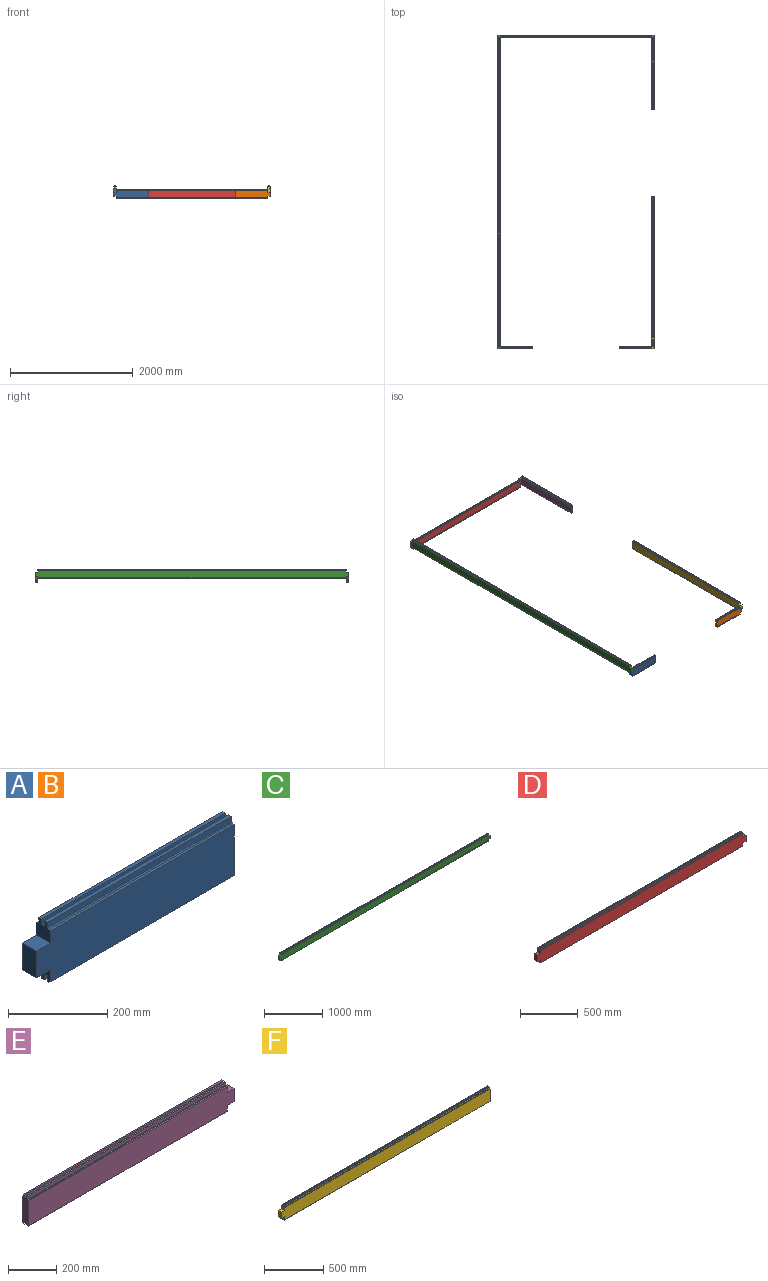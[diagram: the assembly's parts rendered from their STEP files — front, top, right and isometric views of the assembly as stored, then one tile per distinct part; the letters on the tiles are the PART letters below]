
ASSEMBLY  parts=6 mates=16
PART A: 30 faces, bbox 565x40x146 mm
  f0: plane 66x40mm, normal (-1,0,0), area 2640mm2, adj f1,f13,f27,f29
  f1: plane 565x126mm, normal (0,-1,0), area 68790mm2, adj f0,f2,f24,f25,f26,f27,f28,f29
  f2: plane 525x3mm, normal (0,-0.71,-0.71), area 2227.4mm2, adj f1,f3,f25,f26
  f3: plane 525x5mm, normal (0,0,-1), area 2625mm2, adj f2,f4,f25,f26
  f4: plane 525x14mm, normal (0,1,0), area 7350mm2, adj f3,f5,f25,f26
  f5: plane 525x8mm, normal (0,0,-1), area 4200mm2, adj f4,f6,f25,f26
  f6: plane 525x14mm, normal (0,-1,0), area 7350mm2, adj f5,f7,f25,f26
  f7: plane 525x8mm, normal (0,0,-1), area 4200mm2, adj f6,f8,f25,f26
  f8: plane 525x14mm, normal (0,1,0), area 7350mm2, adj f7,f9,f25,f26
  f9: plane 525x8mm, normal (0,0,-1), area 4200mm2, adj f8,f10,f25,f26
  f10: plane 525x14mm, normal (0,-1,0), area 7350mm2, adj f9,f11,f25,f26
  f11: plane 525x5mm, normal (0,0,-1), area 2625mm2, adj f10,f12,f25,f26
  f12: plane 525x3mm, normal (0,0.71,-0.71), area 2227.4mm2, adj f11,f13,f25,f26
  f13: plane 565x126mm, normal (0,1,0), area 68790mm2, adj f0,f12,f14,f25,f26,f27,f28,f29
  f14: plane 525x3mm, normal (0,0.71,0.71), area 2227.4mm2, adj f13,f15,f25,f28
  f15: plane 525x5mm, normal (0,0,1), area 2625mm2, adj f14,f16,f25,f28
  f16: plane 525x14mm, normal (0,1,0), area 7350mm2, adj f15,f17,f25,f28
  f17: plane 525x8mm, normal (0,0,1), area 4200mm2, adj f16,f18,f25,f28
  f18: plane 525x14mm, normal (0,-1,0), area 7350mm2, adj f17,f19,f25,f28
  f19: plane 525x8mm, normal (0,0,1), area 4200mm2, adj f18,f20,f25,f28
  f20: plane 525x14mm, normal (0,1,0), area 7350mm2, adj f19,f21,f25,f28
  f21: plane 525x8mm, normal (0,0,1), area 4200mm2, adj f20,f22,f25,f28
  f22: plane 525x14mm, normal (0,-1,0), area 7350mm2, adj f21,f23,f25,f28
  f23: plane 525x5mm, normal (0,0,1), area 2625mm2, adj f22,f24,f25,f28
  f24: plane 525x3mm, normal (0,-0.71,0.71), area 2227.4mm2, adj f1,f23,f25,f28
  f25: plane 146x40mm, normal (1,0,0), area 5262mm2, adj f1,f2,f3,f4,f5,f6,f7,f8
  f26: plane 40x33mm, normal (-1,0,0), area 1087mm2, adj f1,f2,f3,f4,f5,f6,f7,f8
  f27: plane 40x40mm, normal (0,0,-1), area 1600mm2, adj f0,f1,f13,f26
  f28: plane 47x40mm, normal (-1,0,0), area 1535mm2, adj f1,f13,f14,f15,f16,f17,f18,f19
  f29: plane 40x40mm, normal (0,0,1), area 1600mm2, adj f0,f1,f13,f28
PART B: same geometry as A
PART C: 34 faces, bbox 5100x40x146 mm
  f0: plane 5100x126mm, normal (0,1,0), area 637800mm2, adj f1,f23,f24,f25,f26,f27,f28,f29
  f1: plane 5020x3mm, normal (0,0.71,0.71), area 21298.1mm2, adj f0,f2,f26,f32
  f2: plane 5020x5mm, normal (0,0,1), area 25100mm2, adj f1,f3,f26,f32
  f3: plane 5020x14mm, normal (0,1,0), area 70280mm2, adj f2,f4,f26,f32
  f4: plane 5020x8mm, normal (0,0,1), area 40160mm2, adj f3,f5,f26,f32
  f5: plane 5020x14mm, normal (0,-1,0), area 70280mm2, adj f4,f6,f26,f32
  f6: plane 5020x8mm, normal (0,0,1), area 40160mm2, adj f5,f7,f26,f32
  f7: plane 5020x14mm, normal (0,1,0), area 70280mm2, adj f6,f8,f26,f32
  f8: plane 5020x8mm, normal (0,0,1), area 40160mm2, adj f7,f9,f26,f32
  f9: plane 5020x14mm, normal (0,-1,0), area 70280mm2, adj f8,f10,f26,f32
  f10: plane 5020x5mm, normal (0,0,1), area 25100mm2, adj f9,f11,f26,f32
  f11: plane 5020x3mm, normal (0,-0.71,0.71), area 21298.1mm2, adj f10,f12,f26,f32
  f12: plane 5100x126mm, normal (0,-1,0), area 637800mm2, adj f11,f13,f24,f25,f26,f27,f28,f29
  f13: plane 5020x3mm, normal (0,-0.71,-0.71), area 21298.1mm2, adj f12,f14,f28,f30
  f14: plane 5020x5mm, normal (0,0,-1), area 25100mm2, adj f13,f15,f28,f30
  f15: plane 5020x14mm, normal (0,1,0), area 70280mm2, adj f14,f16,f28,f30
  f16: plane 5020x8mm, normal (0,0,-1), area 40160mm2, adj f15,f17,f28,f30
  f17: plane 5020x14mm, normal (0,-1,0), area 70280mm2, adj f16,f18,f28,f30
  f18: plane 5020x8mm, normal (0,0,-1), area 40160mm2, adj f17,f19,f28,f30
  f19: plane 5020x14mm, normal (0,1,0), area 70280mm2, adj f18,f20,f28,f30
  f20: plane 5020x8mm, normal (0,0,-1), area 40160mm2, adj f19,f21,f28,f30
  f21: plane 5020x14mm, normal (0,-1,0), area 70280mm2, adj f20,f22,f28,f30
  f22: plane 5020x5mm, normal (0,0,-1), area 25100mm2, adj f21,f23,f28,f30
  f23: plane 5020x3mm, normal (0,0.71,-0.71), area 21298.1mm2, adj f0,f22,f28,f30
  f24: plane 66x40mm, normal (1,0,0), area 2640mm2, adj f0,f12,f31,f33
  f25: plane 66x40mm, normal (-1,0,0), area 2640mm2, adj f0,f12,f27,f29
  f26: plane 47x40mm, normal (-1,0,0), area 1535mm2, adj f0,f1,f2,f3,f4,f5,f6,f7
  f27: plane 40x40mm, normal (0,0,1), area 1600mm2, adj f0,f12,f25,f26
  f28: plane 40x33mm, normal (-1,0,0), area 1087mm2, adj f0,f12,f13,f14,f15,f16,f17,f18
  f29: plane 40x40mm, normal (0,0,-1), area 1600mm2, adj f0,f12,f25,f28
  f30: plane 40x33mm, normal (1,0,0), area 1087mm2, adj f0,f12,f13,f14,f15,f16,f17,f18
  f31: plane 40x40mm, normal (0,0,-1), area 1600mm2, adj f0,f12,f24,f30
  f32: plane 47x40mm, normal (1,0,0), area 1535mm2, adj f0,f1,f2,f3,f4,f5,f6,f7
  f33: plane 40x40mm, normal (0,0,1), area 1600mm2, adj f0,f12,f24,f32
PART D: 34 faces, bbox 2550x40x146 mm
  f0: plane 2550x126mm, normal (0,1,0), area 316500mm2, adj f1,f13,f14,f25,f26,f27,f28,f29
  f1: plane 2470x3mm, normal (0,0.71,0.71), area 10479.3mm2, adj f0,f2,f27,f33
  f2: plane 2470x5mm, normal (0,0,1), area 12350mm2, adj f1,f3,f27,f33
  f3: plane 2470x14mm, normal (0,1,0), area 34580mm2, adj f2,f4,f27,f33
  f4: plane 2470x8mm, normal (0,0,1), area 19760mm2, adj f3,f5,f27,f33
  f5: plane 2470x14mm, normal (0,-1,0), area 34580mm2, adj f4,f6,f27,f33
  f6: plane 2470x8mm, normal (0,0,1), area 19760mm2, adj f5,f7,f27,f33
  f7: plane 2470x14mm, normal (0,1,0), area 34580mm2, adj f6,f8,f27,f33
  f8: plane 2470x8mm, normal (0,0,1), area 19760mm2, adj f7,f9,f27,f33
  f9: plane 2470x14mm, normal (0,-1,0), area 34580mm2, adj f8,f10,f27,f33
  f10: plane 2470x5mm, normal (0,0,1), area 12350mm2, adj f9,f11,f27,f33
  f11: plane 2470x3mm, normal (0,-0.71,0.71), area 10479.3mm2, adj f10,f12,f27,f33
  f12: plane 2550x126mm, normal (0,-1,0), area 316500mm2, adj f11,f13,f14,f15,f26,f27,f28,f29
  f13: plane 66x40mm, normal (1,0,0), area 2640mm2, adj f0,f12,f30,f32
  f14: plane 66x40mm, normal (-1,0,0), area 2640mm2, adj f0,f12,f26,f29
  f15: plane 2470x3mm, normal (0,-0.71,-0.71), area 10479.3mm2, adj f12,f16,f28,f31
  f16: plane 2470x5mm, normal (0,0,-1), area 12350mm2, adj f15,f17,f28,f31
  f17: plane 2470x14mm, normal (0,1,0), area 34580mm2, adj f16,f18,f28,f31
  f18: plane 2470x8mm, normal (0,0,-1), area 19760mm2, adj f17,f19,f28,f31
  f19: plane 2470x14mm, normal (0,-1,0), area 34580mm2, adj f18,f20,f28,f31
  f20: plane 2470x8mm, normal (0,0,-1), area 19760mm2, adj f19,f21,f28,f31
  f21: plane 2470x14mm, normal (0,1,0), area 34580mm2, adj f20,f22,f28,f31
  f22: plane 2470x8mm, normal (0,0,-1), area 19760mm2, adj f21,f23,f28,f31
  f23: plane 2470x14mm, normal (0,-1,0), area 34580mm2, adj f22,f24,f28,f31
  f24: plane 2470x5mm, normal (0,0,-1), area 12350mm2, adj f23,f25,f28,f31
  f25: plane 2470x3mm, normal (0,0.71,-0.71), area 10479.3mm2, adj f0,f24,f28,f31
  f26: plane 40x40mm, normal (0,0,1), area 1600mm2, adj f0,f12,f14,f27
  f27: plane 47x40mm, normal (-1,0,0), area 1535mm2, adj f0,f1,f2,f3,f4,f5,f6,f7
  f28: plane 40x33mm, normal (-1,0,0), area 1087mm2, adj f0,f12,f15,f16,f17,f18,f19,f20
  f29: plane 40x40mm, normal (0,0,-1), area 1600mm2, adj f0,f12,f14,f28
  f30: plane 40x40mm, normal (0,0,-1), area 1600mm2, adj f0,f12,f13,f31
  f31: plane 40x33mm, normal (1,0,0), area 1087mm2, adj f0,f12,f15,f16,f17,f18,f19,f20
  f32: plane 40x40mm, normal (0,0,1), area 1600mm2, adj f0,f12,f13,f33
  f33: plane 47x40mm, normal (1,0,0), area 1535mm2, adj f0,f1,f2,f3,f4,f5,f6,f7
PART E: 30 faces, bbox 1200x40x146 mm
  f0: plane 1200x126mm, normal (0,1,0), area 148800mm2, adj f1,f13,f24,f25,f26,f27,f28,f29
  f1: plane 1160x3mm, normal (0,0.71,0.71), area 4921.5mm2, adj f0,f2,f25,f29
  f2: plane 1160x5mm, normal (0,0,1), area 5800mm2, adj f1,f3,f25,f29
  f3: plane 1160x14mm, normal (0,1,0), area 16240mm2, adj f2,f4,f25,f29
  f4: plane 1160x8mm, normal (0,0,1), area 9280mm2, adj f3,f5,f25,f29
  f5: plane 1160x14mm, normal (0,-1,0), area 16240mm2, adj f4,f6,f25,f29
  f6: plane 1160x8mm, normal (0,0,1), area 9280mm2, adj f5,f7,f25,f29
  f7: plane 1160x14mm, normal (0,1,0), area 16240mm2, adj f6,f8,f25,f29
  f8: plane 1160x8mm, normal (0,0,1), area 9280mm2, adj f7,f9,f25,f29
  f9: plane 1160x14mm, normal (0,-1,0), area 16240mm2, adj f8,f10,f25,f29
  f10: plane 1160x5mm, normal (0,0,1), area 5800mm2, adj f9,f11,f25,f29
  f11: plane 1160x3mm, normal (0,-0.71,0.71), area 4921.5mm2, adj f10,f12,f25,f29
  f12: plane 1200x126mm, normal (0,-1,0), area 148800mm2, adj f11,f13,f14,f25,f26,f27,f28,f29
  f13: plane 66x40mm, normal (1,0,0), area 2640mm2, adj f0,f12,f26,f28
  f14: plane 1160x3mm, normal (0,-0.71,-0.71), area 4921.5mm2, adj f12,f15,f25,f27
  f15: plane 1160x5mm, normal (0,0,-1), area 5800mm2, adj f14,f16,f25,f27
  f16: plane 1160x14mm, normal (0,1,0), area 16240mm2, adj f15,f17,f25,f27
  f17: plane 1160x8mm, normal (0,0,-1), area 9280mm2, adj f16,f18,f25,f27
  f18: plane 1160x14mm, normal (0,-1,0), area 16240mm2, adj f17,f19,f25,f27
  f19: plane 1160x8mm, normal (0,0,-1), area 9280mm2, adj f18,f20,f25,f27
  f20: plane 1160x14mm, normal (0,1,0), area 16240mm2, adj f19,f21,f25,f27
  f21: plane 1160x8mm, normal (0,0,-1), area 9280mm2, adj f20,f22,f25,f27
  f22: plane 1160x14mm, normal (0,-1,0), area 16240mm2, adj f21,f23,f25,f27
  f23: plane 1160x5mm, normal (0,0,-1), area 5800mm2, adj f22,f24,f25,f27
  f24: plane 1160x3mm, normal (0,0.71,-0.71), area 4921.5mm2, adj f0,f23,f25,f27
  f25: plane 146x40mm, normal (-1,0,0), area 5262mm2, adj f0,f1,f2,f3,f4,f5,f6,f7
  f26: plane 40x40mm, normal (0,0,-1), area 1600mm2, adj f0,f12,f13,f27
  f27: plane 40x33mm, normal (1,0,0), area 1087mm2, adj f0,f12,f14,f15,f16,f17,f18,f19
  f28: plane 40x40mm, normal (0,0,1), area 1600mm2, adj f0,f12,f13,f29
  f29: plane 47x40mm, normal (1,0,0), area 1535mm2, adj f0,f1,f2,f3,f4,f5,f6,f7
PART F: 30 faces, bbox 2480x40x146 mm
  f0: plane 66x40mm, normal (-1,0,0), area 2640mm2, adj f1,f13,f27,f28
  f1: plane 2480x126mm, normal (0,1,0), area 310080mm2, adj f0,f2,f24,f25,f26,f27,f28,f29
  f2: plane 2440x3mm, normal (0,0.71,0.71), area 10352mm2, adj f1,f3,f25,f29
  f3: plane 2440x5mm, normal (0,0,1), area 12200mm2, adj f2,f4,f25,f29
  f4: plane 2440x14mm, normal (0,1,0), area 34160mm2, adj f3,f5,f25,f29
  f5: plane 2440x8mm, normal (0,0,1), area 19520mm2, adj f4,f6,f25,f29
  f6: plane 2440x14mm, normal (0,-1,0), area 34160mm2, adj f5,f7,f25,f29
  f7: plane 2440x8mm, normal (0,0,1), area 19520mm2, adj f6,f8,f25,f29
  f8: plane 2440x14mm, normal (0,1,0), area 34160mm2, adj f7,f9,f25,f29
  f9: plane 2440x8mm, normal (0,0,1), area 19520mm2, adj f8,f10,f25,f29
  f10: plane 2440x14mm, normal (0,-1,0), area 34160mm2, adj f9,f11,f25,f29
  f11: plane 2440x5mm, normal (0,0,1), area 12200mm2, adj f10,f12,f25,f29
  f12: plane 2440x3mm, normal (0,-0.71,0.71), area 10352mm2, adj f11,f13,f25,f29
  f13: plane 2480x126mm, normal (0,-1,0), area 310080mm2, adj f0,f12,f14,f25,f26,f27,f28,f29
  f14: plane 2440x3mm, normal (0,-0.71,-0.71), area 10352mm2, adj f13,f15,f25,f26
  f15: plane 2440x5mm, normal (0,0,-1), area 12200mm2, adj f14,f16,f25,f26
  f16: plane 2440x14mm, normal (0,1,0), area 34160mm2, adj f15,f17,f25,f26
  f17: plane 2440x8mm, normal (0,0,-1), area 19520mm2, adj f16,f18,f25,f26
  f18: plane 2440x14mm, normal (0,-1,0), area 34160mm2, adj f17,f19,f25,f26
  f19: plane 2440x8mm, normal (0,0,-1), area 19520mm2, adj f18,f20,f25,f26
  f20: plane 2440x14mm, normal (0,1,0), area 34160mm2, adj f19,f21,f25,f26
  f21: plane 2440x8mm, normal (0,0,-1), area 19520mm2, adj f20,f22,f25,f26
  f22: plane 2440x14mm, normal (0,-1,0), area 34160mm2, adj f21,f23,f25,f26
  f23: plane 2440x5mm, normal (0,0,-1), area 12200mm2, adj f22,f24,f25,f26
  f24: plane 2440x3mm, normal (0,0.71,-0.71), area 10352mm2, adj f1,f23,f25,f26
  f25: plane 146x40mm, normal (1,0,0), area 5262mm2, adj f1,f2,f3,f4,f5,f6,f7,f8
  f26: plane 40x33mm, normal (-1,0,0), area 1087mm2, adj f1,f13,f14,f15,f16,f17,f18,f19
  f27: plane 40x40mm, normal (0,0,-1), area 1600mm2, adj f0,f1,f13,f26
  f28: plane 40x40mm, normal (0,0,1), area 1600mm2, adj f0,f1,f13,f29
  f29: plane 47x40mm, normal (-1,0,0), area 1535mm2, adj f1,f2,f3,f4,f5,f6,f7,f8
PLACE A at identity fixed
PLACE B rot(axis=(0,0,1),180deg) t=(1420,0,0)mm
PLACE C rot(axis=(0,0,1),90deg) t=(-545,2530,73)mm
PLACE D rot(axis=(-0.11,0.09,-0.99),0deg) t=(710,5060,0)mm
PLACE E rot(axis=(0,0,1),90deg) t=(1965,4480,66)mm
PLACE F rot(axis=(0,0,1),90deg) t=(1965,1220,66)mm
MATE planar B.f0 <-> E.f12  axis (1,0,0) through (1985,0,0)mm
MATE planar C.f31 <-> A.f29  axis (0,0,-1) through (-545,5060,33)mm
MATE planar C.f12 <-> A.f28  axis (1,0,0) through (-525,2530,66)mm
MATE planar B.f28 <-> F.f1  axis (1,0,0) through (1945,0,52.84)mm
MATE planar F.f26 <-> B.f1  axis (0,-1,0) through (1965,20,18.59)mm
MATE planar D.f33 <-> E.f0  axis (1,0,0) through (1945,5060,52.84)mm
MATE planar D.f27 <-> C.f12  axis (-1,0,0) through (-525,5060,52.84)mm
MATE planar E.f27 <-> D.f12  axis (0,1,0) through (1965,5040,18.59)mm
MATE planar D.f26 <-> C.f31  axis (0,0,1) through (-545,5060,33)mm
MATE planar B.f7 <-> A.f7  axis (0,0,-1) through (1682.5,0,-66)mm
MATE planar C.f30 <-> D.f12  axis (0,1,0) through (-545,5040,18.59)mm
MATE planar C.f28 <-> A.f13  axis (0,-1,0) through (-545,20,18.59)mm
MATE planar B.f0 <-> E.f12  axis (1,0,0) through (1985,0,0)mm
MATE planar B.f13 <-> A.f1  axis (0,-1,0) through (1693.34,-20,0)mm
MATE planar E.f26 <-> D.f32  axis (0,0,-1) through (1965,5060,33)mm
MATE planar B.f29 <-> F.f27  axis (0,0,1) through (1965,0,33)mm
